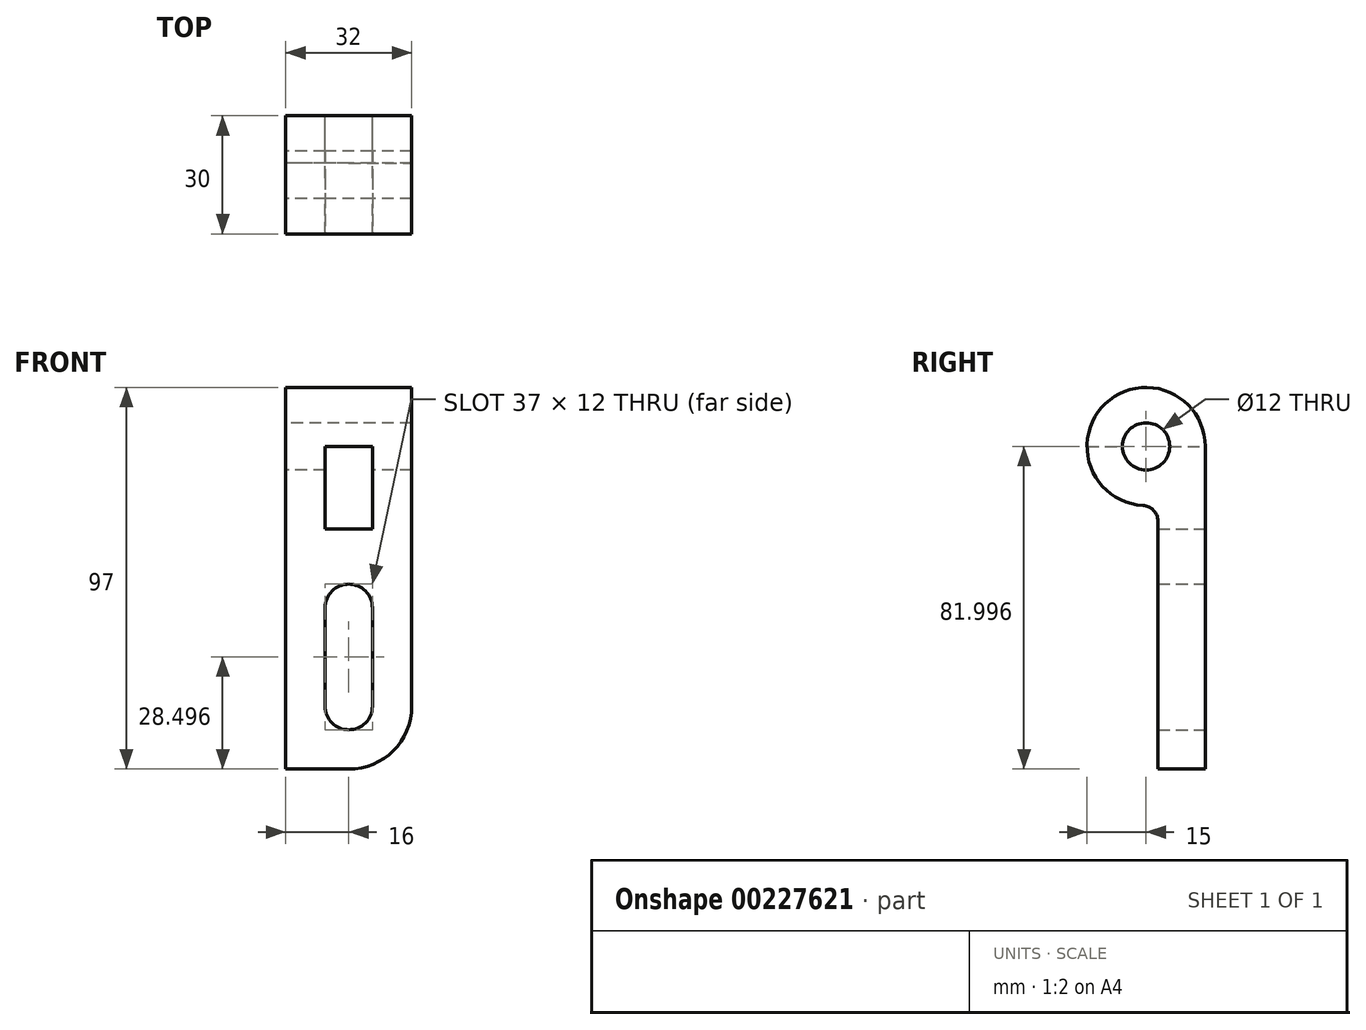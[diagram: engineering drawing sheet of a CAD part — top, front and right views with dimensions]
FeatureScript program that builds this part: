
annotation { "Feature Type Name" : "Feature", "Feature Type Description" : "" }
export const myFeature = defineFeature(function(context is Context, id is Id, definition is map)
    precondition{}
    {
        {
            var Q0;
            Q0=qCreatedBy(makeId("Right.planeOp"),FACE);
            var sketch = newSketch(context, id + "F0", { "sketchPlane" : qUnion([Q0])});
            skArc(sketch, "E0", {"start": v(0, 35.52) * mm, "mid": v(-25.32, 46.4) * mm, "end": v(-15.79, 20.54) * mm});
            skCircle(sketch, "E1", {"center": v(-15, 35.52) * mm, "radius": 6 * mm});
            skLineSegment(sketch, "E2", {"start": v(0, 35.52) * mm, "end": v(0, -46.48) * mm});
            skLineSegment(sketch, "E3", {"start": v(0, -46.48) * mm, "end": v(-12, -46.48) * mm});
            skLineSegment(sketch, "E4", {"start": v(-12, -46.48) * mm, "end": v(-12, 16.54) * mm});
            skPoint(sketch, "E5.visualSharp", {"position": v(-12, 20.82) * mm});
            skArc(sketch, "E5.filletArc", {"start": v(-12, 16.54) * mm, "mid": v(-13.1, 19.3) * mm, "end": v(-15.79, 20.54) * mm});
            skSolve(sketch);
        }
        {
            var Q0;
            Q0=makeQuery(id+"F0.imprint","IMPRINT",FACE,{"disambiguationData":[TD([[makeQuery(id+"F0.imprint","IMPRINT",EDGE,{"derivedFrom":sQuery(id+"F0.wireOp",EDGE,"E0")}),1.0]])]});
            extrude(context, id + "F1", {"entities" : qUnion([Q0]), "depth" : 32 * mm});
        }
        {
            var Q0;
            Q0=qCreatedBy(makeId("Front.planeOp"),FACE);
            var sketch = newSketch(context, id + "F2", { "sketchPlane" : qUnion([Q0])});
            skLineSegment(sketch, "E6.0", {"start": v(32, -46.48) * mm, "end": v(0, -46.48) * mm});
            skLineSegment(sketch, "E6.1", {"start": v(0, 16.54) * mm, "end": v(0, 20.54) * mm});
            skLineSegment(sketch, "E6.2", {"start": v(21.12, 20.54) * mm, "end": v(0, 20.54) * mm});
            skLineSegment(sketch, "E6.3", {"start": v(32, 16.54) * mm, "end": v(0, 16.54) * mm});
            skLineSegment(sketch, "E6.4", {"start": v(0, 50.52) * mm, "end": v(0, 20.54) * mm});
            skLineSegment(sketch, "E6.6", {"start": v(32, 35.52) * mm, "end": v(0, 35.52) * mm});
            skLineSegment(sketch, "E6.7", {"start": v(0, -46.48) * mm, "end": v(0, 16.54) * mm});
            skLineSegment(sketch, "E6.8", {"start": v(0, 41.52) * mm, "end": v(0, 29.52) * mm});
            skLineSegment(sketch, "E6.9", {"start": v(0, 35.52) * mm, "end": v(0, -30.48) * mm});
            skLineSegment(sketch, "E7.0", {"start": v(32, -46.48) * mm, "end": v(32, 16.54) * mm});
            skLineSegment(sketch, "E7.1", {"start": v(32, 35.52) * mm, "end": v(32, -30.48) * mm});
            skLineSegment(sketch, "E7.2", {"start": v(32, 16.54) * mm, "end": v(32, 20.54) * mm});
            skArc(sketch, "E8", {"start": v(10, -30.48) * mm, "mid": v(16, -36.48) * mm, "end": v(22, -30.48) * mm});
            skPoint(sketch, "E8.centerSnap0", {"position": v(16, -46.48) * mm});
            skArc(sketch, "E9", {"start": v(22, -5.48) * mm, "mid": v(16, 0.52) * mm, "end": v(10, -5.48) * mm});
            skLineSegment(sketch, "E10", {"start": v(10, -5.48) * mm, "end": v(10, -30.48) * mm});
            skLineSegment(sketch, "E11", {"start": v(22, -5.48) * mm, "end": v(22, -30.48) * mm});
            skArc(sketch, "E12", {"start": v(0, -30.48) * mm, "mid": v(16, -46.48) * mm, "end": v(32, -30.48) * mm});
            skPoint(sketch, "E13.orphan", {"position": v(0, -46.48) * mm});
            skPoint(sketch, "E14.orphan", {"position": v(32, -46.48) * mm});
            skLineSegment(sketch, "E15", {"start": v(10, 14.52) * mm, "end": v(10, 50.52) * mm});
            skLineSegment(sketch, "E16", {"start": v(22, -5.48) * mm, "end": v(22, -5.48) * mm});
            skLineSegment(sketch, "E17", {"start": v(0, 50.52) * mm, "end": v(32, 50.52) * mm});
            skLineSegment(sketch, "E18", {"start": v(10, 50.52) * mm, "end": v(22, 50.52) * mm});
            skLineSegment(sketch, "E19", {"start": v(10, 14.52) * mm, "end": v(22, 14.52) * mm});
            skLineSegment(sketch, "E20.trimOffspring", {"start": v(22, 14.52) * mm, "end": v(22, 50.52) * mm});
            skLineSegment(sketch, "E21", {"start": v(0, -30.48) * mm, "end": v(0, -46.48) * mm});
            skLineSegment(sketch, "E22", {"start": v(0, -46.48) * mm, "end": v(32, -46.48) * mm});
            skLineSegment(sketch, "E23", {"start": v(32, -30.48) * mm, "end": v(31.22, -35.4) * mm});
            skSolve(sketch);
        }
        {
            var Q0;
            {var subQ4=sQuery(id+"F2.wireOp",EDGE,"E20.trimOffspring");var subQ6=sQuery(id+"F2.wireOp",EDGE,"E6.3");var subQ8=makeQuery(id+"F2.imprint","INTERSECT",VERTEX,{"derivedFrom":[subQ6,subQ4]});Q0=makeQuery(id+"F2.imprint","IMPRINT",FACE,{"disambiguationData":[TD([[makeQuery(id+"F2.imprint","IMPRINT",EDGE,{"disambiguationData":[TD([[subQ8,-1.0]])],"derivedFrom":subQ6}),-1.0]])]});}
            var Q1;
            {var subQ5=sQuery(id+"F2.wireOp",EDGE,"E18");Q1=makeQuery(id+"F2.imprint","IMPRINT",FACE,{"disambiguationData":[TD([[makeQuery(id+"F2.imprint","IMPRINT",EDGE,{"derivedFrom":subQ5}),-1.0]])]});}
            var Q2;
            {var subQ5=sQuery(id+"F2.wireOp",EDGE,"E19");Q2=makeQuery(id+"F2.imprint","IMPRINT",FACE,{"disambiguationData":[TD([[makeQuery(id+"F2.imprint","IMPRINT",EDGE,{"derivedFrom":subQ5}),1.0]])]});}
            var Q3;
            Q3=makeQuery(id+"F2.imprint","IMPRINT",FACE,{"disambiguationData":[TD([[makeQuery(id+"F2.imprint","IMPRINT",EDGE,{"derivedFrom":sQuery(id+"F2.wireOp",EDGE,"E8")}),1.0]])]});
            var Q4;
            {var subQ0=sQuery(id+"F2.wireOp",EDGE,"E7.0");Q4=makeQuery(id+"F2.imprint","IMPRINT",FACE,{"disambiguationData":[TD([[makeQuery(id+"F2.imprint","IMPRINT",EDGE,{"derivedFrom":subQ0}),1.0]])]});}
            var Q5;
            {var subQ0=sQuery(id+"F2.wireOp",EDGE,"E21");Q5=makeQuery(id+"F2.imprint","IMPRINT",FACE,{"disambiguationData":[TD([[makeQuery(id+"F2.imprint","IMPRINT",EDGE,{"derivedFrom":subQ0}),1.0]])]});}
            extrude(context, id + "F3", {"entities" : qUnion([Q0, Q1, Q2, Q3, Q4, Q5]), "operationType" : NewBodyOperationType.REMOVE, "endBound" : BoundingType.THROUGH_ALL, "depth" : 25 * mm});
        }
    });
